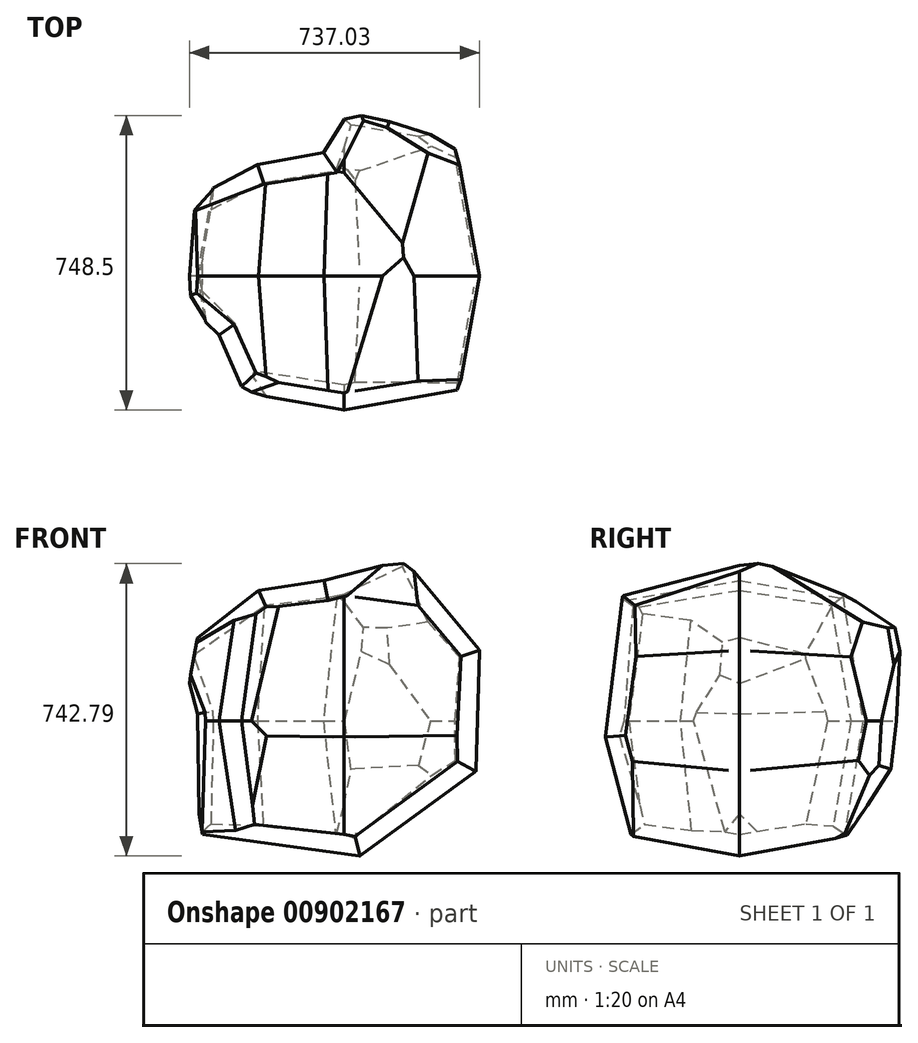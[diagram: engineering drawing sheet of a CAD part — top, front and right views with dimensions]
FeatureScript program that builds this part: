
annotation { "Feature Type Name" : "Feature", "Feature Type Description" : "" }
export const myFeature = defineFeature(function(context is Context, id is Id, definition is map)
    precondition{}
    {
        {
            var Q0;
            Q0=qCreatedBy(makeId("Front.planeOp"),FACE);
            var sketch = newSketch(context, id + "F0", { "sketchPlane" : qUnion([Q0])});
            skLineSegment(sketch, "E0", {"start": v(-414.16, 175.05) * mm, "end": v(-371.65, 18.17) * mm});
            skLineSegment(sketch, "E1", {"start": v(-371.82, 19.4) * mm, "end": v(-367.4, -282.27) * mm});
            skLineSegment(sketch, "E2", {"start": v(-363.09, -287.15) * mm, "end": v(38.72, -342.6) * mm});
            skLineSegment(sketch, "E3", {"start": v(42.35, -341.69) * mm, "end": v(333.36, -129.23) * mm});
            skLineSegment(sketch, "E4", {"start": v(335.41, -125.34) * mm, "end": v(344.3, 178.16) * mm});
            skLineSegment(sketch, "E5", {"start": v(343.16, 181.5) * mm, "end": v(154.16, 409.45) * mm});
            skLineSegment(sketch, "E6", {"start": v(154.16, 409.45) * mm, "end": v(-50.82, 357.25) * mm});
            skLineSegment(sketch, "E7", {"start": v(-50.33, 357.35) * mm, "end": v(-216.45, 332.5) * mm});
            skLineSegment(sketch, "E8", {"start": v(-216.45, 332.5) * mm, "end": v(-412.4, 180.3) * mm});
            skPoint(sketch, "E9.visualSharp", {"position": v(-415.03, 178.26) * mm});
            skArc(sketch, "E9.filletArc", {"start": v(-412.4, 180.3) * mm, "mid": v(-414.08, 177.94) * mm, "end": v(-414.16, 175.05) * mm});
            skPoint(sketch, "E10.visualSharp", {"position": v(-50.58, 357.31) * mm});
            skArc(sketch, "E10.filletArc", {"start": v(-50.82, 357.25) * mm, "mid": v(-48.6, 347.5) * mm, "end": v(-50.33, 357.35) * mm});
            skPoint(sketch, "E11.visualSharp", {"position": v(344.36, 180.04) * mm});
            skArc(sketch, "E11.filletArc", {"start": v(344.3, 178.16) * mm, "mid": v(344.04, 179.93) * mm, "end": v(343.16, 181.5) * mm});
            skPoint(sketch, "E12.visualSharp", {"position": v(335.34, -127.79) * mm});
            skArc(sketch, "E12.filletArc", {"start": v(333.36, -129.23) * mm, "mid": v(334.84, -127.52) * mm, "end": v(335.41, -125.34) * mm});
            skPoint(sketch, "E13.visualSharp", {"position": v(40.72, -342.88) * mm});
            skArc(sketch, "E13.filletArc", {"start": v(38.72, -342.6) * mm, "mid": v(40.62, -342.5) * mm, "end": v(42.35, -341.69) * mm});
            skPoint(sketch, "E14.visualSharp", {"position": v(-367.34, -286.57) * mm});
            skArc(sketch, "E14.filletArc", {"start": v(-367.4, -282.27) * mm, "mid": v(-366.15, -285.51) * mm, "end": v(-363.09, -287.15) * mm});
            skPoint(sketch, "E15.visualSharp", {"position": v(-371.81, 18.78) * mm});
            skArc(sketch, "E15.filletArc", {"start": v(-371.65, 18.17) * mm, "mid": v(-361.87, 20.18) * mm, "end": v(-371.82, 19.4) * mm});
            skCircle(sketch, "E16", {"center": v(0, 0) * mm, "radius": 500 * mm, "construction": true});
            skSolve(sketch);
        }
        {
            var Q0;
            Q0=qSketchRegion(id+"F0",true);
            extrude(context, id + "F1", {"entities" : qUnion([Q0]), "endBound" : BoundingType.SYMMETRIC, "depth" : 1000 * mm, "offsetDistance" : 25 * mm, "hasDraft" : true, "draftAngle" : 10 * degree, "draftPullDirection" : true});
        }
        {
            var Q0;
            Q0=qCreatedBy(makeId("Right.planeOp"),FACE);
            var sketch = newSketch(context, id + "F2", { "sketchPlane" : qUnion([Q0])});
            skLineSegment(sketch, "E17", {"start": v(-296.83, 316.57) * mm, "end": v(-340.51, -39.34) * mm});
            skLineSegment(sketch, "E18", {"start": v(-340.39, -41.2) * mm, "end": v(-261.07, -346.85) * mm});
            skLineSegment(sketch, "E19", {"start": v(-261.07, -346.85) * mm, "end": v(45.56, -391.45) * mm});
            skLineSegment(sketch, "E20", {"start": v(48.32, -391.06) * mm, "end": v(271.1, -291.27) * mm});
            skLineSegment(sketch, "E21", {"start": v(273.17, -289.54) * mm, "end": v(386.56, -124.78) * mm});
            skLineSegment(sketch, "E22", {"start": v(387.42, -122.42) * mm, "end": v(420.9, 230.3) * mm});
            skLineSegment(sketch, "E23", {"start": v(418.36, 235.13) * mm, "end": v(66.5, 432.6) * mm});
            skLineSegment(sketch, "E24", {"start": v(62.55, 433.01) * mm, "end": v(-293.37, 320.73) * mm});
            skPoint(sketch, "E25.visualSharp", {"position": v(-296.44, 319.76) * mm});
            skArc(sketch, "E25.filletArc", {"start": v(-293.37, 320.73) * mm, "mid": v(-295.71, 319.16) * mm, "end": v(-296.83, 316.57) * mm});
            skPoint(sketch, "E26.visualSharp", {"position": v(-340.63, -40.28) * mm});
            skArc(sketch, "E26.filletArc", {"start": v(-340.51, -39.34) * mm, "mid": v(-340.54, -40.28) * mm, "end": v(-340.39, -41.2) * mm});
            skPoint(sketch, "E27.visualSharp", {"position": v(272.37, -290.7) * mm});
            skArc(sketch, "E27.filletArc", {"start": v(271.1, -291.27) * mm, "mid": v(272.25, -290.55) * mm, "end": v(273.17, -289.54) * mm});
            skPoint(sketch, "E28.visualSharp", {"position": v(387.3, -123.71) * mm});
            skArc(sketch, "E28.filletArc", {"start": v(386.56, -124.78) * mm, "mid": v(387.14, -123.66) * mm, "end": v(387.42, -122.42) * mm});
            skPoint(sketch, "E29.visualSharp", {"position": v(421.2, 233.54) * mm});
            skArc(sketch, "E29.filletArc", {"start": v(420.9, 230.3) * mm, "mid": v(420.34, 233.09) * mm, "end": v(418.36, 235.13) * mm});
            skPoint(sketch, "E30.visualSharp", {"position": v(64.61, 433.66) * mm});
            skArc(sketch, "E30.filletArc", {"start": v(66.5, 432.6) * mm, "mid": v(64.57, 433.22) * mm, "end": v(62.55, 433.01) * mm});
            skPoint(sketch, "E31.visualSharp", {"position": v(47, -391.66) * mm});
            skArc(sketch, "E31.filletArc", {"start": v(45.56, -391.45) * mm, "mid": v(46.97, -391.45) * mm, "end": v(48.32, -391.06) * mm});
            skCircle(sketch, "E32", {"center": v(0, 0) * mm, "radius": 500 * mm, "construction": true});
            skSolve(sketch);
        }
        {
            var Q0;
            Q0=qSketchRegion(id+"F2",true);
            extrude(context, id + "F3", {"entities" : qUnion([Q0]), "operationType" : NewBodyOperationType.INTERSECT, "endBound" : BoundingType.SYMMETRIC, "depth" : 1000 * mm, "offsetDistance" : 25 * mm, "hasDraft" : true, "draftAngle" : 10 * degree, "draftPullDirection" : true});
        }
        {
            var Q0;
            Q0=qCreatedBy(makeId("Top.planeOp"),FACE);
            var sketch = newSketch(context, id + "F4", { "sketchPlane" : qUnion([Q0])});
            skLineSegment(sketch, "E33", {"start": v(-317.21, -149.57) * mm, "end": v(-410.48, -57.8) * mm});
            skLineSegment(sketch, "E34", {"start": v(-317.21, -149.57) * mm, "end": v(-260.8, -281.05) * mm});
            skLineSegment(sketch, "E35", {"start": v(-260.8, -281.05) * mm, "end": v(-45.5, -387.37) * mm});
            skLineSegment(sketch, "E36", {"start": v(-45.5, -387.37) * mm, "end": v(329.36, -291.86) * mm});
            skLineSegment(sketch, "E37", {"start": v(445.8, 77.15) * mm, "end": v(329.36, -291.86) * mm});
            skLineSegment(sketch, "E38", {"start": v(445.8, 77.15) * mm, "end": v(384, 262.52) * mm});
            skLineSegment(sketch, "E39", {"start": v(384, 262.52) * mm, "end": v(126.68, 415.3) * mm});
            skLineSegment(sketch, "E40", {"start": v(30.92, 444.83) * mm, "end": v(126.68, 415.3) * mm});
            skLineSegment(sketch, "E41", {"start": v(30.92, 444.83) * mm, "end": v(-52.21, 313.2) * mm});
            skLineSegment(sketch, "E42", {"start": v(-52.21, 313.2) * mm, "end": v(-220.05, 282.96) * mm});
            skLineSegment(sketch, "E43", {"start": v(-220.05, 282.96) * mm, "end": v(-406.9, 184.25) * mm});
            skLineSegment(sketch, "E44", {"start": v(-406.9, 184.25) * mm, "end": v(-408.8, 55.97) * mm});
            skLineSegment(sketch, "E45", {"start": v(-410.48, -57.8) * mm, "end": v(-408.8, 55.97) * mm});
            skCircle(sketch, "E46", {"center": v(0, 0) * mm, "radius": 500 * mm, "construction": true});
            skSolve(sketch);
        }
        {
            var Q0;
            Q0=qSketchRegion(id+"F4",true);
            extrude(context, id + "F5", {"entities" : qUnion([Q0]), "operationType" : NewBodyOperationType.INTERSECT, "endBound" : BoundingType.SYMMETRIC, "depth" : 1000 * mm, "offsetDistance" : 25 * mm, "hasDraft" : true, "draftAngle" : 10 * degree, "draftPullDirection" : true});
        }
    });
